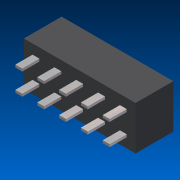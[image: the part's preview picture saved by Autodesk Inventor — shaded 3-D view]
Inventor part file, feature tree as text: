
AUTODESK INVENTOR PART (.ipt)
format: ipt  version: 2015 SP1 (Build 190203100, 203)  size: 187,904 bytes
history: native  units: mm
features: extrude x3, sketch x3, other x1
ambient origin geometry x8: Origin, YZ Plane, XZ Plane, XY Plane, X Axis, Y Axis, Z Axis, Center Point
bodies: Body1 (feature_tree)
feature tree (7):
  other  "Твердое тело1"
  extrude  "Выдавливание1"  Depth=13.0mm
  extrude  "Выдавливание2"  Depth=5.08mm
  extrude  "Выдавливание3"  Depth=4.4mm TaperAngle=0.0deg
  sketch  "Эскиз1"
  sketch  "Эскиз2"
  sketch  "Эскиз3"
